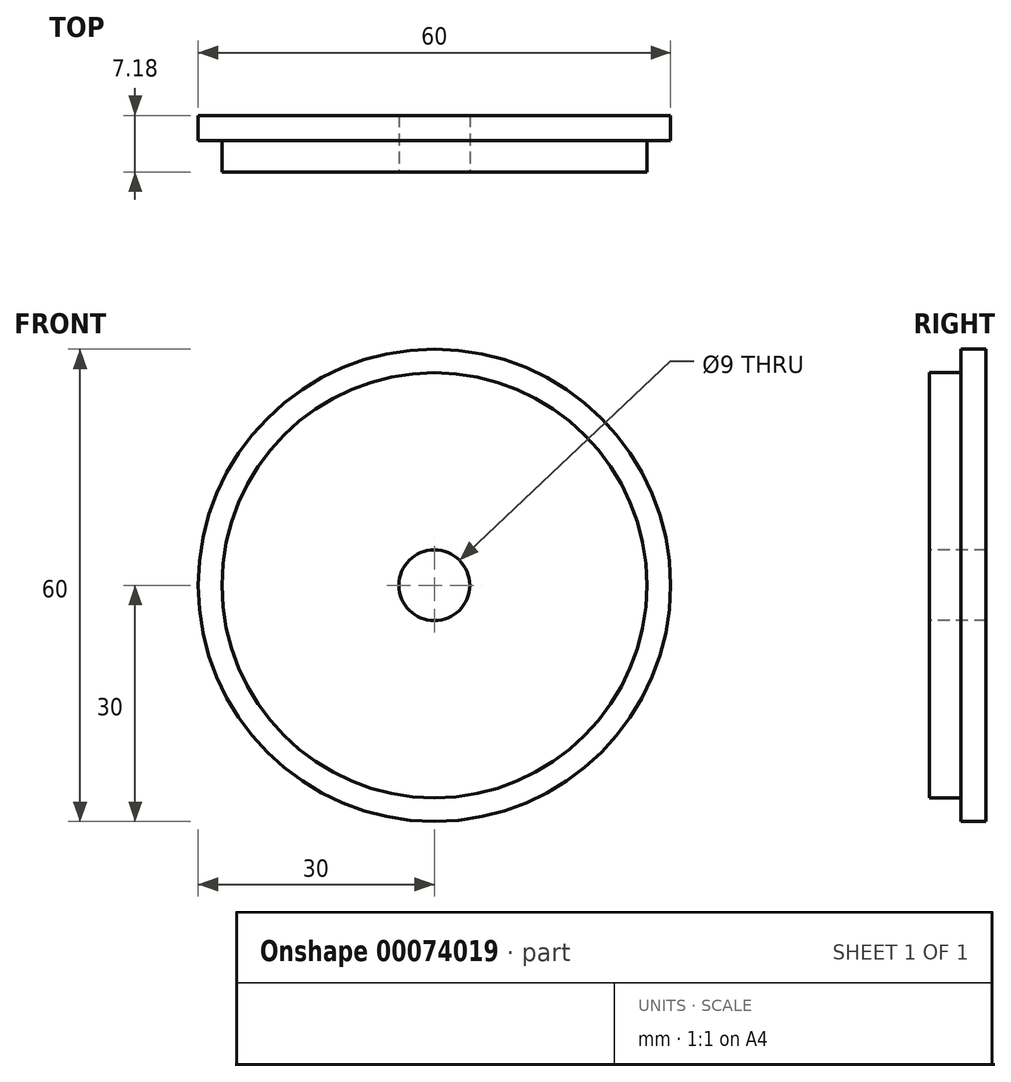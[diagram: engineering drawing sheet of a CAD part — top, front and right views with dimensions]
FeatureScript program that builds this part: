
annotation { "Feature Type Name" : "Feature", "Feature Type Description" : "" }
export const myFeature = defineFeature(function(context is Context, id is Id, definition is map)
    precondition{}
    {
        {
            var Q0;
            Q0=qCreatedBy(makeId("Front.planeOp"),FACE);
            var sketch = newSketch(context, id + "F0", { "sketchPlane" : qUnion([Q0])});
            skCircle(sketch, "E0", {"center": v(0, 0) * mm, "radius": 30 * mm});
            skSolve(sketch);
        }
        {
            var Q0;
            Q0 = qSketchRegion(id + "F0", true);
            extrude(context, id + "F1", {"entities" : qUnion([Q0]), "depth" : 3.17 * mm});
        }
        {
            var Q0;
            Q0=makeQuery(id+"F1.opExtrude","CAP_FACE",FACE,{"disambiguationData":[OSD([sQuery(id+"F0.wireOp",EDGE,"E0")])],"isStart":false});
            var sketch = newSketch(context, id + "F2", { "sketchPlane" : qUnion([Q0])});
            skCircle(sketch, "E1", {"center": v(0, 0) * mm, "radius": 27 * mm});
            skSolve(sketch);
        }
        {
            var Q0;
            Q0=makeQuery(id+"F2.imprint","IMPRINT",FACE,{"disambiguationData":[TD([[makeQuery(id+"F2.imprint","IMPRINT",EDGE,{"derivedFrom":sQuery(id+"F2.wireOp",EDGE,"E1")}),1.0]])]});
            extrude(context, id + "F3", {"entities" : qUnion([Q0]), "operationType" : NewBodyOperationType.ADD, "depth" : 4 * mm});
        }
        {
            var Q0;
            Q0=makeQuery(id+"F3.opExtrude","CAP_FACE",FACE,{"disambiguationData":[OSD([sQuery(id+"F2.wireOp",EDGE,"E1")])],"isStart":false});
            var sketch = newSketch(context, id + "F4", { "sketchPlane" : qUnion([Q0])});
            skCircle(sketch, "E2", {"center": v(0, 0) * mm, "radius": 4.5 * mm});
            skSolve(sketch);
        }
        {
            var Q0;
            Q0=makeQuery(id+"F4.imprint","IMPRINT",FACE,{"disambiguationData":[TD([[makeQuery(id+"F4.imprint","IMPRINT",EDGE,{"derivedFrom":sQuery(id+"F4.wireOp",EDGE,"E2")}),1.0]])]});
            extrude(context, id + "F5", {"entities" : qUnion([Q0]), "operationType" : NewBodyOperationType.REMOVE, "endBound" : BoundingType.THROUGH_ALL, "oppositeDirection" : true, "depth" : 25.4 * mm});
        }
    });
